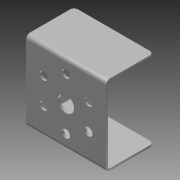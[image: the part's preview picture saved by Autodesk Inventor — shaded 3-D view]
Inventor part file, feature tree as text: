
AUTODESK INVENTOR PART (.ipt)
format: ipt  version: 2014 (Build 180170000, 170)  size: 147,456 bytes
history: native  units: in
note: dims shown in document units (in); Inventor stores cm internally (conversion verified against a paired STEP export)
features: sheet_metal_op x6, other x3, sketch x2, fillet x1
ambient origin geometry x8: Origin, YZ Plane, XZ Plane, XY Plane, X Axis, Y Axis, Z Axis, Center Point
bodies: Body1 (feature_tree)
feature tree (12):
  sheet_metal_op  "Face2"
  sheet_metal_op  "Face3"
  sheet_metal_op  "Flange1"
  fillet  "Fillet1"  Radius=5.0in
  other  "Plate2"
  sketch  "Sketch3"  dims[d1=1.0in]
  other  "Plate3"
  sheet_metal_op  "Bend1"
  sketch  "Sketch4"  dims[d2=0.5in d3=1.625in d8=0.125in d19=0.125in d20=2.3622in d22=360.0deg d24=0.125in d25=0.125in d26=0.0625in d27=0.25in d28=0.125in d29=0.125in d30=0.0625in d31=0.25in d32=0.125in d33=1.0in d34=90.0deg d35=0.125in d36=0.5in d37=0.125in d38=0.125in d39=0.25in]
  other  "Plate4"
  sheet_metal_op  "Bend2"
  sheet_metal_op  "Corner1"
